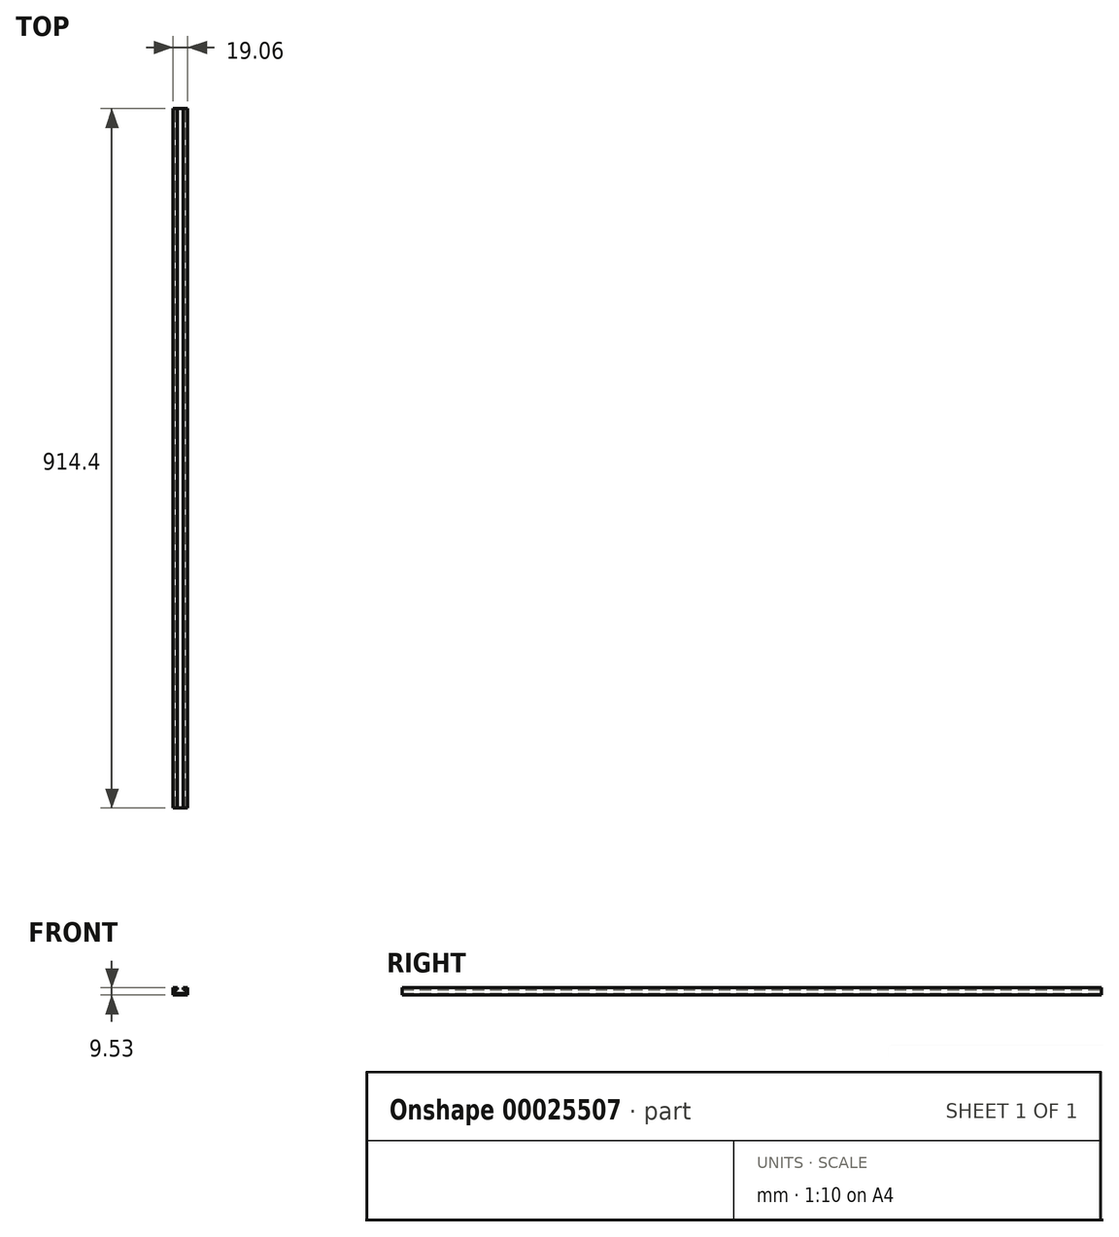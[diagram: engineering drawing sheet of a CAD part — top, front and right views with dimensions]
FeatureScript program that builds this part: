
annotation { "Feature Type Name" : "Feature", "Feature Type Description" : "" }
export const myFeature = defineFeature(function(context is Context, id is Id, definition is map)
    precondition{}
    {
        {
            var Q0;
            Q0=qCreatedBy(makeId("Front.planeOp"),FACE);
            var sketch = newSketch(context, id + "F0", { "sketchPlane" : qUnion([Q0])});
            skLineSegment(sketch, "E0.bottom", {"start": v(-9.53, 0) * mm, "end": v(9.53, 0) * mm});
            skLineSegment(sketch, "E0.top", {"start": v(-9.53, 9.53) * mm, "end": v(-3.81, 9.53) * mm});
            skLineSegment(sketch, "E0.left", {"start": v(-9.53, 0) * mm, "end": v(-9.53, 9.53) * mm});
            skLineSegment(sketch, "E0.right", {"start": v(9.53, 0) * mm, "end": v(9.52, 9.53) * mm});
            skLineSegment(sketch, "E1.bottom", {"start": v(-7.5, 2.03) * mm, "end": v(7.5, 2.03) * mm});
            skLineSegment(sketch, "E1.top", {"start": v(-7.5, 7.5) * mm, "end": v(-3.81, 7.5) * mm});
            skLineSegment(sketch, "E1.left", {"start": v(-7.5, 2.03) * mm, "end": v(-7.5, 7.5) * mm});
            skLineSegment(sketch, "E1.right", {"start": v(7.5, 2.03) * mm, "end": v(7.5, 7.5) * mm});
            skLineSegment(sketch, "E2", {"start": v(-3.81, 9.53) * mm, "end": v(-3.81, 7.5) * mm});
            skLineSegment(sketch, "E3", {"start": v(3.8, 7.5) * mm, "end": v(3.8, 9.53) * mm});
            skLineSegment(sketch, "E4.trimOffspring", {"start": v(3.8, 9.53) * mm, "end": v(9.52, 9.53) * mm});
            skLineSegment(sketch, "E5.trimOffspring", {"start": v(3.8, 7.5) * mm, "end": v(7.5, 7.5) * mm});
            skSolve(sketch);
        }
        {
            var Q0;
            Q0 = qSketchRegion(id + "F0", true);
            extrude(context, id + "F1", {"entities" : qUnion([Q0]), "endBound" : BoundingType.SYMMETRIC, "depth" : 914.4 * mm, "hasSecondDirection" : true, "secondDirectionOppositeDirection" : true, "secondDirectionDepth" : 25.4 * mm});
        }
    });
